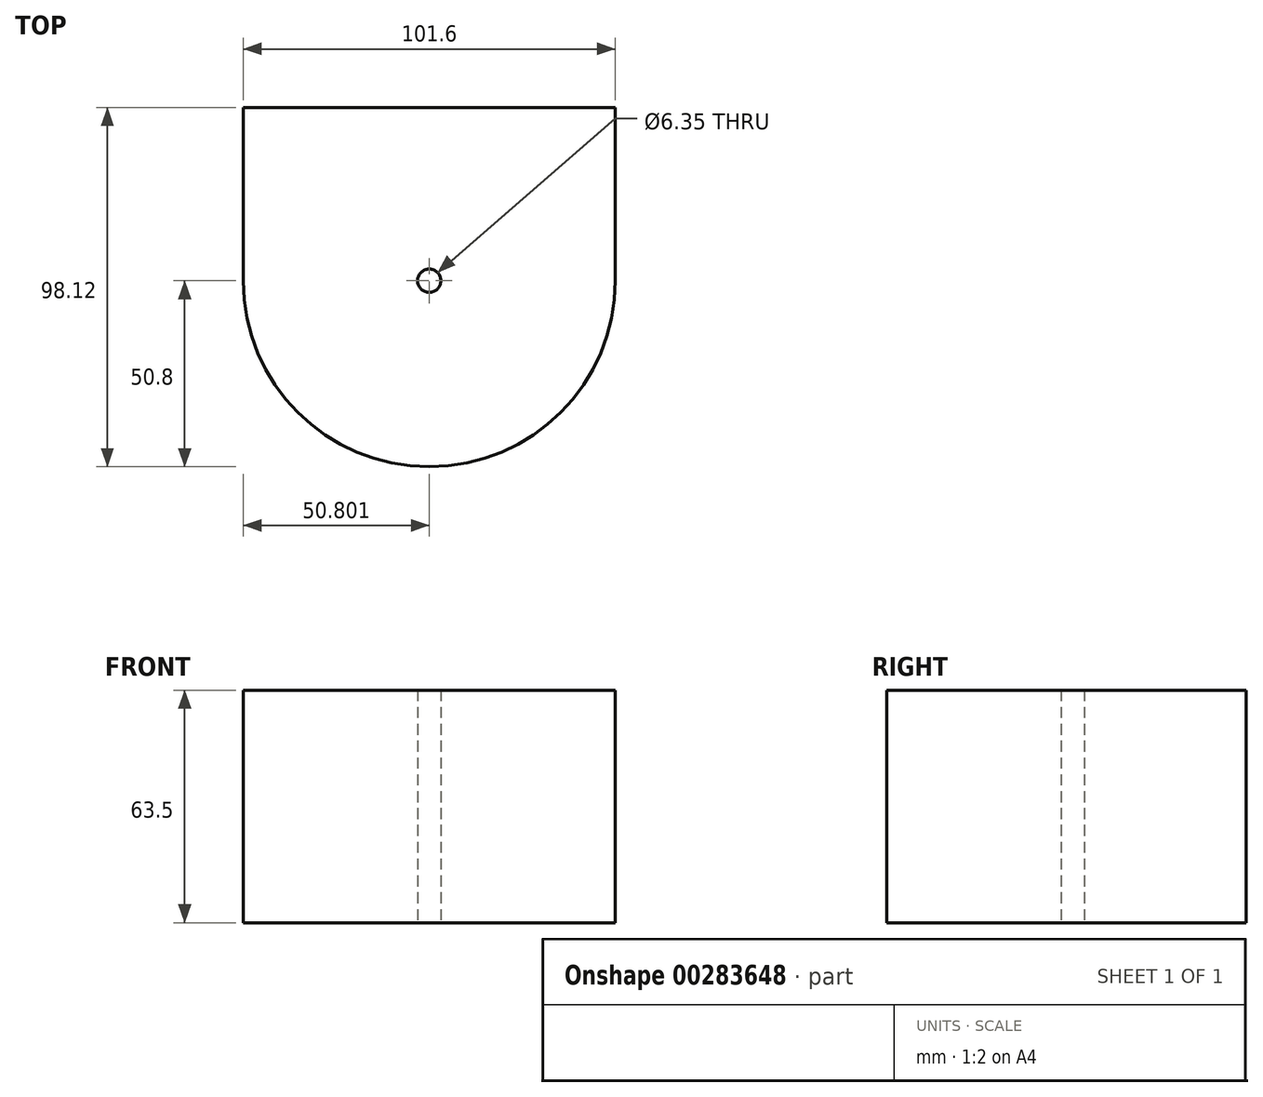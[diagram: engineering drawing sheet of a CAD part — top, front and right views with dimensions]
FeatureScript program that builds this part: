
annotation { "Feature Type Name" : "Feature", "Feature Type Description" : "" }
export const myFeature = defineFeature(function(context is Context, id is Id, definition is map)
    precondition{}
    {
        {
            var Q0;
            Q0=qCreatedBy(makeId("Front.planeOp"),FACE);
            var sketch = newSketch(context, id + "F0", { "sketchPlane" : qUnion([Q0])});
            skLineSegment(sketch, "E0.bottom", {"start": v(76.03, 0) * mm, "end": v(-25.57, 0) * mm});
            skLineSegment(sketch, "E0.top", {"start": v(76.03, -63.5) * mm, "end": v(-25.57, -63.5) * mm});
            skLineSegment(sketch, "E0.left", {"start": v(76.03, 0) * mm, "end": v(76.03, -63.5) * mm});
            skLineSegment(sketch, "E0.right", {"start": v(-25.57, 0) * mm, "end": v(-25.57, -63.5) * mm});
            skSolve(sketch);
        }
        {
            var Q0;
            Q0 = qSketchRegion(id + "F0", true);
            extrude(context, id + "F1", {"entities" : qUnion([Q0]), "endBound" : BoundingType.SYMMETRIC, "depth" : 98.12 * mm});
        }
        {
            var Q0;
            Q0=makeQuery(id+"F1.opExtrude","SWEPT_FACE",FACE,{"disambiguationData":[OSD([sQuery(id+"F0.wireOp",EDGE,"E0.bottom")])]});
            var sketch = newSketch(context, id + "F2", { "sketchPlane" : qUnion([Q0])});
            skLineSegment(sketch, "E1", {"start": v(-25.57, 49.06) * mm, "end": v(76.03, 49.06) * mm});
            skLineSegment(sketch, "E2", {"start": v(76.03, 49.06) * mm, "end": v(76.03, 1.74) * mm});
            skLineSegment(sketch, "E3", {"start": v(76.03, 1.74) * mm, "end": v(-25.57, 1.74) * mm});
            skArc(sketch, "E4", {"start": v(-25.57, 1.74) * mm, "mid": v(25.23, -49.06) * mm, "end": v(76.03, 1.74) * mm});
            skSolve(sketch);
        }
        {
            var Q0;
            {var subQ0=sQuery(id+"F2.wireOp",EDGE,"E4");var subQ1=sQuery(id+"F0.wireOp",EDGE,"E0.bottom");var subQ4=makeQuery(id+"F1.opExtrude","CAP_EDGE",EDGE,{"disambiguationData":[OSD([subQ1])],"isStart":false});var subQ5=makeQuery(id+"F2.imprint","INTERSECT",VERTEX,{"derivedFrom":[subQ4,subQ0]});Q0=makeQuery(id+"F2.imprint","IMPRINT",FACE,{"disambiguationData":[TD([[makeQuery(id+"F2.imprint","IMPRINT",EDGE,{"disambiguationData":[TD([[subQ5,-1.0]])],"derivedFrom":subQ4}),-1.0]])]});}
            var Q1;
            {var subQ0=sQuery(id+"F2.wireOp",EDGE,"E4");var subQ1=sQuery(id+"F0.wireOp",EDGE,"E0.bottom");var subQ4=makeQuery(id+"F1.opExtrude","CAP_EDGE",EDGE,{"disambiguationData":[OSD([subQ1])],"isStart":false});var subQ5=makeQuery(id+"F2.imprint","INTERSECT",VERTEX,{"derivedFrom":[subQ4,subQ0]});Q1=makeQuery(id+"F2.imprint","IMPRINT",FACE,{"disambiguationData":[TD([[makeQuery(id+"F2.imprint","IMPRINT",EDGE,{"disambiguationData":[TD([[subQ5,1.0]])],"derivedFrom":subQ4}),-1.0]])]});}
            extrude(context, id + "F3", {"entities" : qUnion([Q0, Q1]), "operationType" : NewBodyOperationType.REMOVE, "endBound" : BoundingType.THROUGH_ALL, "oppositeDirection" : true, "depth" : 25.4 * mm});
        }
        {
            var Q0;
            Q0=makeQuery(id+"F1.opExtrude","SWEPT_FACE",FACE,{"disambiguationData":[OSD([sQuery(id+"F0.wireOp",EDGE,"E0.top")])]});
            var sketch = newSketch(context, id + "F4", { "sketchPlane" : qUnion([Q0])});
            skCircle(sketch, "E5", {"center": v(25.23, -1.74) * mm, "radius": 30.83 * mm});
            skSolve(sketch);
        }
        {
            var Q0;
            Q0=sQuery(id+"F4.wireOp",VERTEX,"E5.center");
            var Q1;
            Q1=makeQuery(id+"F1.opExtrude","SWEPT_BODY",BODY,{"disambiguationData":[OSD([sQuery(id+"F0.wireOp",EDGE,"E0.bottom"),sQuery(id+"F0.wireOp",EDGE,"E0.top"),sQuery(id+"F0.wireOp",EDGE,"E0.left"),sQuery(id+"F0.wireOp",EDGE,"E0.right")])]});
            hole(context, id + "F5", {"style" : HoleStyle.SIMPLE, "endStyle" : HoleEndStyle.THROUGH, "holeDiameter" : 6.35 * mm, "tappedDepth" : 12.7 * mm, "tapClearance" : 3, "locations" : qUnion([Q0]), "scope" : qUnion([Q1])});
        }
    });
